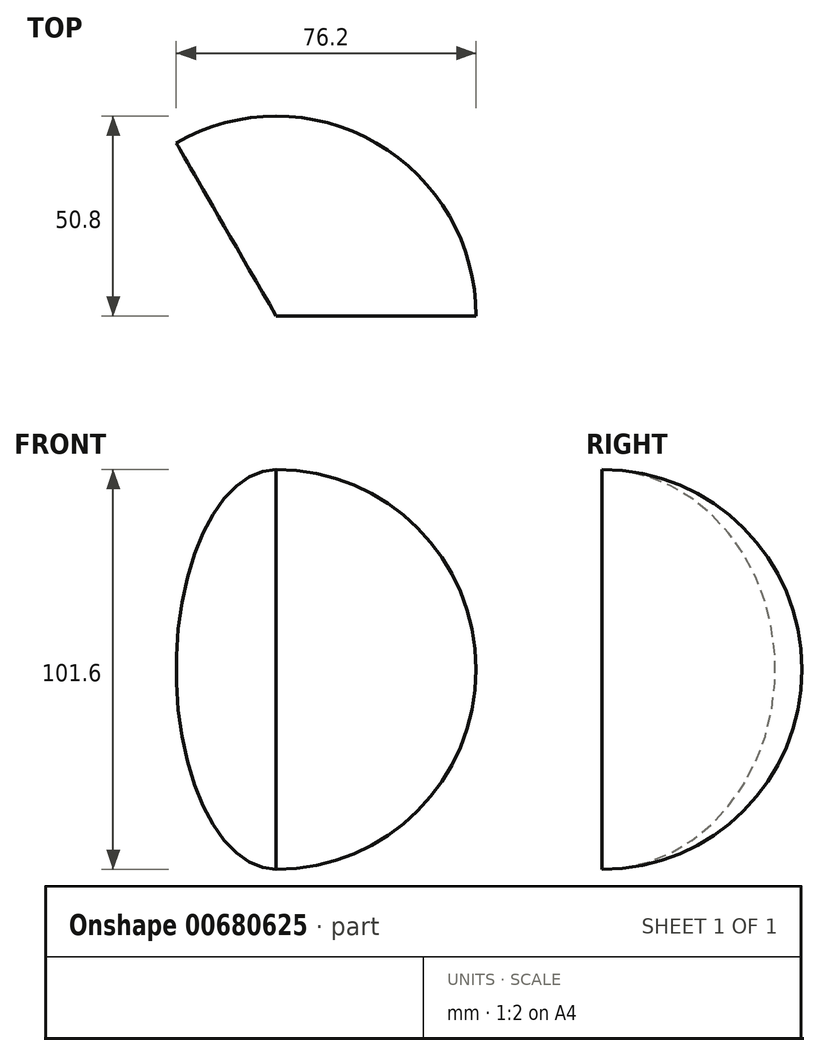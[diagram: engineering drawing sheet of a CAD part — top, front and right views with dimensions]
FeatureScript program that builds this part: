
annotation { "Feature Type Name" : "Feature", "Feature Type Description" : "" }
export const myFeature = defineFeature(function(context is Context, id is Id, definition is map)
    precondition{}
    {
        {
            var Q0;
            Q0=qCreatedBy(makeId("Front.planeOp"),FACE);
            var sketch = newSketch(context, id + "F0", { "sketchPlane" : qUnion([Q0])});
            skArc(sketch, "E0", {"start": v(0, -50.8) * mm, "mid": v(50.8, 0) * mm, "end": v(0, 50.8) * mm});
            skLineSegment(sketch, "E1", {"start": v(0, 0) * mm, "end": v(0, 70.25) * mm, "construction": true});
            skLineSegment(sketch, "E2", {"start": v(0, 50.8) * mm, "end": v(0, -50.8) * mm});
            skSolve(sketch);
        }
        {
            var Q0;
            Q0=makeQuery(id+"F0.imprint","IMPRINT",FACE,{"disambiguationData":[TD([[makeQuery(id+"F0.imprint","IMPRINT",EDGE,{"derivedFrom":sQuery(id+"F0.wireOp",EDGE,"E0")}),1.0]])]});
            var Q1;
            Q1=sQuery(id+"F0.wireOp",EDGE,"E0");
            var Q2;
            Q2=sQuery(id+"F0.wireOp",EDGE,"E1");
            revolve(context, id + "F1", {"entities" : qUnion([Q0]), "surfaceEntities" : qUnion([Q1]), "axis" : qUnion([Q2]), "revolveType" : RevolveType.ONE_DIRECTION, "angle" : 120 * degree});
        }
    });
